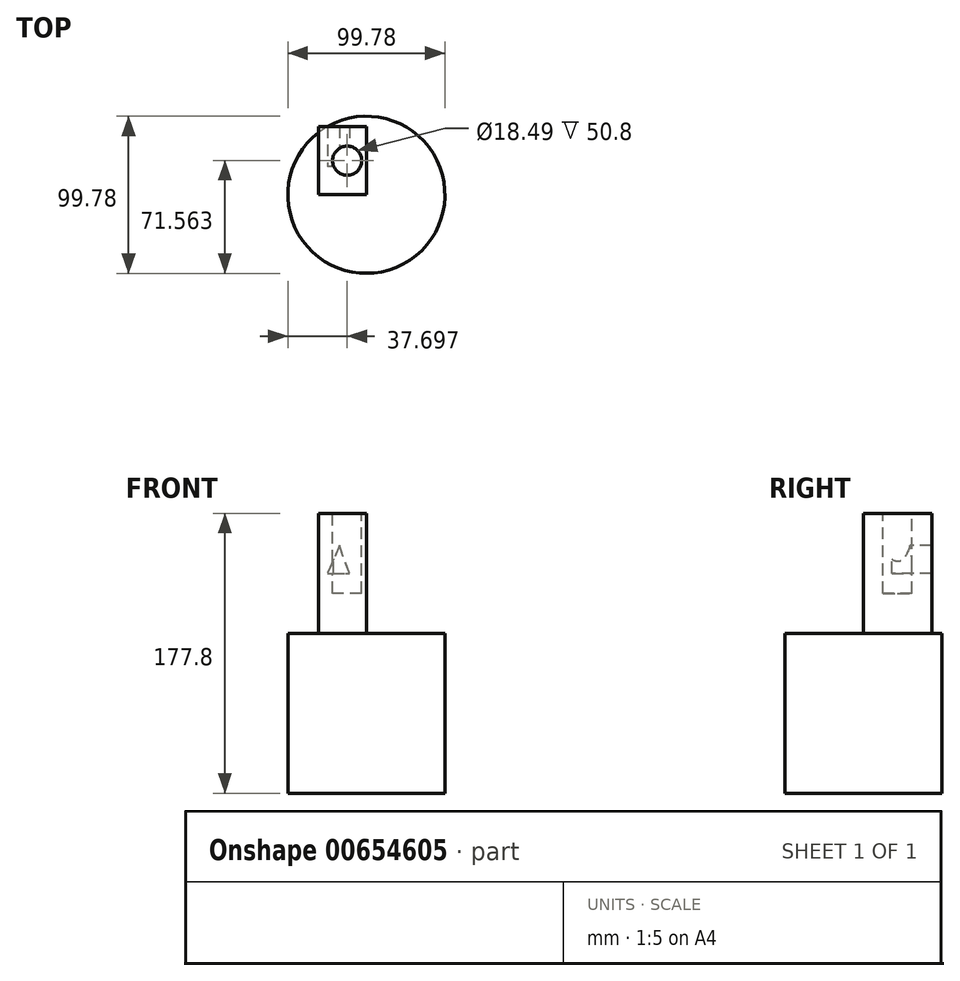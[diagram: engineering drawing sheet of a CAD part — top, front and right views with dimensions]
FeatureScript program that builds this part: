
annotation { "Feature Type Name" : "Feature", "Feature Type Description" : "" }
export const myFeature = defineFeature(function(context is Context, id is Id, definition is map)
    precondition{}
    {
        {
            var Q0;
            Q0=qCreatedBy(makeId("Top.planeOp"),FACE);
            var sketch = newSketch(context, id + "F0", { "sketchPlane" : qUnion([Q0])});
            skCircle(sketch, "E0", {"center": v(0, 0) * mm, "radius": 49.89 * mm});
            skSolve(sketch);
        }
        {
            var Q0;
            Q0 = qSketchRegion(id + "F0", true);
            extrude(context, id + "F1", {"entities" : qUnion([Q0]), "depth" : 101.6 * mm, "offsetDistance" : 25.4 * mm});
        }
        {
            var Q0;
            Q0=makeQuery(id+"F1.opExtrude","CAP_FACE",FACE,{"disambiguationData":[OSD([sQuery(id+"F0.wireOp",EDGE,"E0")])],"isStart":false});
            var sketch = newSketch(context, id + "F2", { "sketchPlane" : qUnion([Q0])});
            skLineSegment(sketch, "E1.bottom", {"start": v(0, 0) * mm, "end": v(-30.43, 0) * mm});
            skLineSegment(sketch, "E1.top", {"start": v(0, 18.01) * mm, "end": v(-30.43, 18.01) * mm});
            skLineSegment(sketch, "E1.left", {"start": v(0, 0) * mm, "end": v(0, 18.01) * mm});
            skLineSegment(sketch, "E1.right", {"start": v(-30.43, 0) * mm, "end": v(-30.43, 18.01) * mm});
            skSolve(sketch);
        }
        {
            var Q0;
            Q0 = qSketchRegion(id + "F2", true);
            extrude(context, id + "F3", {"entities" : qUnion([Q0]), "operationType" : NewBodyOperationType.ADD, "depth" : 76.2 * mm, "offsetDistance" : 25.4 * mm});
        }
        {
            var Q0;
            Q0=makeQuery(id+"F3.opExtrude","SWEPT_FACE",FACE,{"disambiguationData":[OSD([sQuery(id+"F2.wireOp",EDGE,"E1.top")])]});
            var sketch = newSketch(context, id + "F4", { "sketchPlane" : qUnion([Q0])});
            skLineSegment(sketch, "E2", {"start": v(17.12, 157.3) * mm, "end": v(24.6, 139.7) * mm});
            skPoint(sketch, "E2.endSnap0", {"position": v(30.43, 139.7) * mm});
            skLineSegment(sketch, "E3", {"start": v(24.6, 139.7) * mm, "end": v(10.8, 139.7) * mm});
            skLineSegment(sketch, "E4", {"start": v(10.8, 139.7) * mm, "end": v(17.12, 157.3) * mm});
            skSolve(sketch);
        }
        {
            var Q0;
            Q0=makeQuery(id+"F4.imprint","IMPRINT",FACE,{"disambiguationData":[TD([[makeQuery(id+"F4.imprint","IMPRINT",EDGE,{"derivedFrom":sQuery(id+"F4.wireOp",EDGE,"E2")}),1.0]])]});
            extrude(context, id + "F5", {"entities" : qUnion([Q0]), "operationType" : NewBodyOperationType.ADD, "depth" : 25.4 * mm, "offsetDistance" : 25.4 * mm});
        }
        {
            var Q0;
            {var subQ0=sQuery(id+"F2.wireOp",EDGE,"E1.top");Q0=makeQuery(id+"F5.boolean.opBoolean","MERGE",FACE,{"derivedFrom":[makeQuery(id+"F3.opExtrude","CAP_FACE",FACE,{"disambiguationData":[OSD([sQuery(id+"F2.wireOp",EDGE,"E1.bottom"),subQ0,sQuery(id+"F2.wireOp",EDGE,"E1.left"),sQuery(id+"F2.wireOp",EDGE,"E1.right")])],"isStart":false}),makeQuery(id+"F5.opExtrude","SWEPT_FACE",FACE,{"disambiguationData":[OSD([subQ0]),TDD([makeQuery(id+"F4.imprint","IMPRINT",EDGE,{"derivedFrom":makeQuery(id+"F3.opExtrude","CAP_EDGE",EDGE,{"disambiguationData":[OSD([subQ0])],"isStart":false})})])]})]});}
            var sketch = newSketch(context, id + "F6", { "sketchPlane" : qUnion([Q0])});
            skCircle(sketch, "E5", {"center": v(-12.2, 21.67) * mm, "radius": 9.24 * mm});
            skSolve(sketch);
        }
        {
            var Q0;
            Q0 = qSketchRegion(id + "F6", true);
            extrude(context, id + "F7", {"entities" : qUnion([Q0]), "operationType" : NewBodyOperationType.REMOVE, "oppositeDirection" : true, "depth" : 50.8 * mm, "offsetDistance" : 25.4 * mm});
        }
    });
